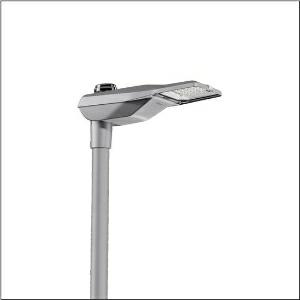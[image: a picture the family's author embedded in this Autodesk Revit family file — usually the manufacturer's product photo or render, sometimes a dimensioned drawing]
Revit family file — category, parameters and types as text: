
# Revit family: streetlight_sl_21_micro___st1_0a_5xe5d67n08db_977e
name_source: partatom
category: Lighting Fixtures
units: mm (PartAtom-declared; Revit-internal decimal feet)

## family parameters
Cut with Voids When Loaded = No
Host = Face
Light Source = No
Part Type = Normal
Room Calculation Point = No
Round Connector Dimension = Use Diameter
Shared = No

## types (1)
- --- (1 x LED, 4580 lm, 39.1 W, 2700K)
    Apparent Load = 39 VA
    CIE Flux Codes = 37 72 97 100 100
    Color Rendering = 70
    Color Temperature = 2700K
    Default Elevation = 1800 mm
    Description = Streetlight SL 21 micro, mast luminaire, primary light control with lens, of PMMA, primary optical cover: cover, of toughened safety glass, transparent, light distribution: ST1.0a, light emission: direct distribution, primary light characteristic: asymmetric, installation type: post-top, LED, 3G 1.5mm², High Power LED, rated luminous flux: 4.580lm, luminous efficacy: 117lm/W, light colour: 727, colour temperature: 2700K, control gear: NEMA (7pin), control: overheat protection, pre-setting: linear dimming characteristic, constant luminous flux control, time-dependent luminous flux control, flexible luminous flux parameterisation, mains connection: 230..240V, AC, 50/60Hz, connection cable pre-assembled, cable length: 6,5m, wiring characteristics: H07RN-F, start of lifetime: 39W, end of service life: 41W, reduction: 18W, luminaire housing, of diecast aluminium (EN AC-44300), powder-coated, SITECO metallic grey (DB 702S), corrosivity category C5 high according to DIN EN ISO 12944, multi-level sealing system, sealing non-destructively replaceable, inclination adjustable: 0°, 5°, 10°, 15°, length: 528mm, width: 235mm, height: 110mm, spigot size: 76/60mm (post-top), mounting height: 4..8m, protection rating (complete): IP66, insulation class (complete): insulation class I (protective earthing), certification: CE, ENEC, ENEC+, VDE, impact resistance: IK10, permissible operating ambient temperature for outdoor applications: -40..+50°C, standard-compliant lighting for roads and squares, packaging unit: 1 piece

Light Distribution: ST1.0a
    Height = 110 mm
    Lamp = 1 x LED
    Lamp Light Flux = 4580 lm
    Lamp Power = 39.1 W
    Lamp count = 1
    Length = 528 mm
    Luminous efficacy = 117 lm/W
    Manufacturer = Siteco
    ModVariant = No
    Model = 5XE5D67N08DB
    Number of Poles = 1
    OnlyDefault = Yes
    Power Factor = 1
    Product Name = Streetlight SL 21 micro | ST1.0a
    Product group = mast luminaire | pylon top
    ProductGroupID = 6100
    Protection Class = Protection class I
    Protection Degree = IP 66
    RLX_Detail_Level = 1
    RLX_Emergency_Light_Flux = 0 lm
    RLX_Emergency_Type = 0
    RLX_Emergency_Type_DB = No
    RlxData = <blob elided: 98753 chars, md5=db510a3c>
    Socket = socket
    Standby Power = 0 W
    System Light Flux = 4580 lm
    System Power = 39 W
    Type Comments = factory setting: luminous flux: 100 % | dim-lin: 254 | 765 mA
    Type Image = l_1294375.jpg
    URL = http://relux.com
    VarID = @adj_135895
    Voltage = 0 V
    Weight = 0.00 kg
    Width = 235 mm

## geometry (parser evidence)
native form markers: Blend x4, Sweep x9
no freeform markers — native parametric forms only
